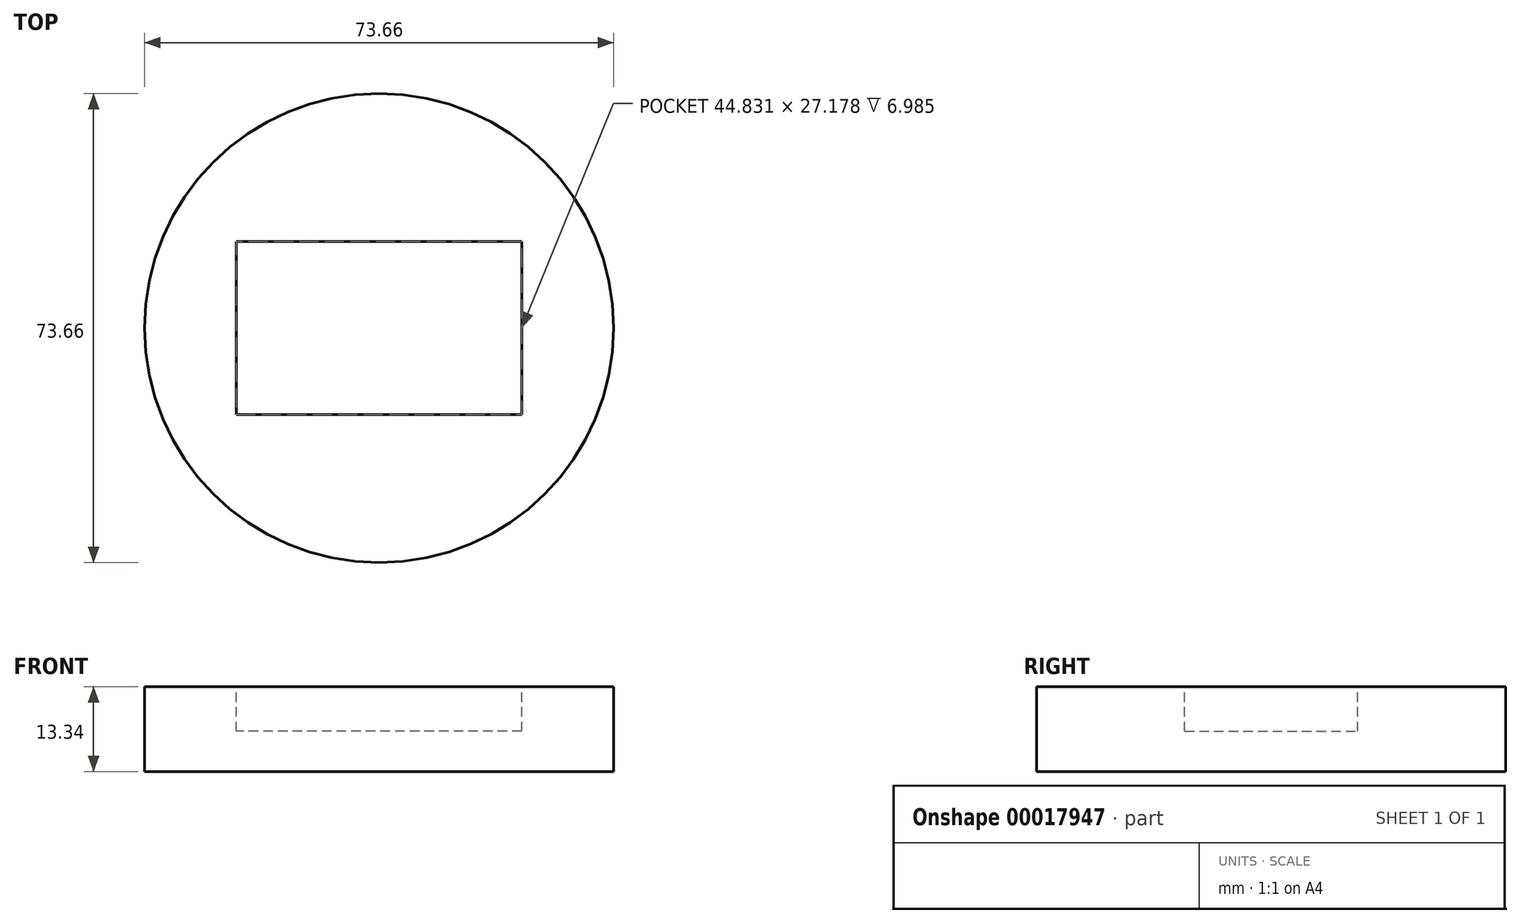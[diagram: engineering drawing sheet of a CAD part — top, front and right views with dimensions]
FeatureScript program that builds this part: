
annotation { "Feature Type Name" : "Feature", "Feature Type Description" : "" }
export const myFeature = defineFeature(function(context is Context, id is Id, definition is map)
    precondition{}
    {
        {
            var Q0;
            Q0=qCreatedBy(makeId("Top.planeOp"),FACE);
            var sketch = newSketch(context, id + "F0", { "sketchPlane" : qUnion([Q0])});
            skCircle(sketch, "E0", {"center": v(0, 0) * mm, "radius": 36.83 * mm});
            skSolve(sketch);
        }
        {
            var Q0;
            Q0 = qSketchRegion(id + "F0", true);
            extrude(context, id + "F1", {"entities" : qUnion([Q0]), "depth" : 13.33 * mm, "offsetDistance" : 25.4 * mm});
        }
        {
            var Q0;
            Q0=makeQuery(id+"F1.opExtrude","CAP_FACE",FACE,{"disambiguationData":[OSD([sQuery(id+"F0.wireOp",EDGE,"E0")])],"isStart":false});
            var sketch = newSketch(context, id + "F2", { "sketchPlane" : qUnion([Q0])});
            skLineSegment(sketch, "E1.bottom", {"start": v(22.42, -13.59) * mm, "end": v(-22.42, -13.59) * mm});
            skLineSegment(sketch, "E1.top", {"start": v(22.42, 13.59) * mm, "end": v(-22.42, 13.59) * mm});
            skLineSegment(sketch, "E1.left", {"start": v(22.42, -13.59) * mm, "end": v(22.42, 13.59) * mm});
            skLineSegment(sketch, "E1.right", {"start": v(-22.42, -13.59) * mm, "end": v(-22.42, 13.59) * mm});
            skPoint(sketch, "E1.middle", {"position": v(0, 0) * mm});
            skSolve(sketch);
        }
        {
            var Q0;
            Q0 = qSketchRegion(id + "F2", true);
            extrude(context, id + "F3", {"entities" : qUnion([Q0]), "operationType" : NewBodyOperationType.REMOVE, "oppositeDirection" : true, "depth" : 7 * mm, "offsetDistance" : 25.4 * mm});
        }
    });
